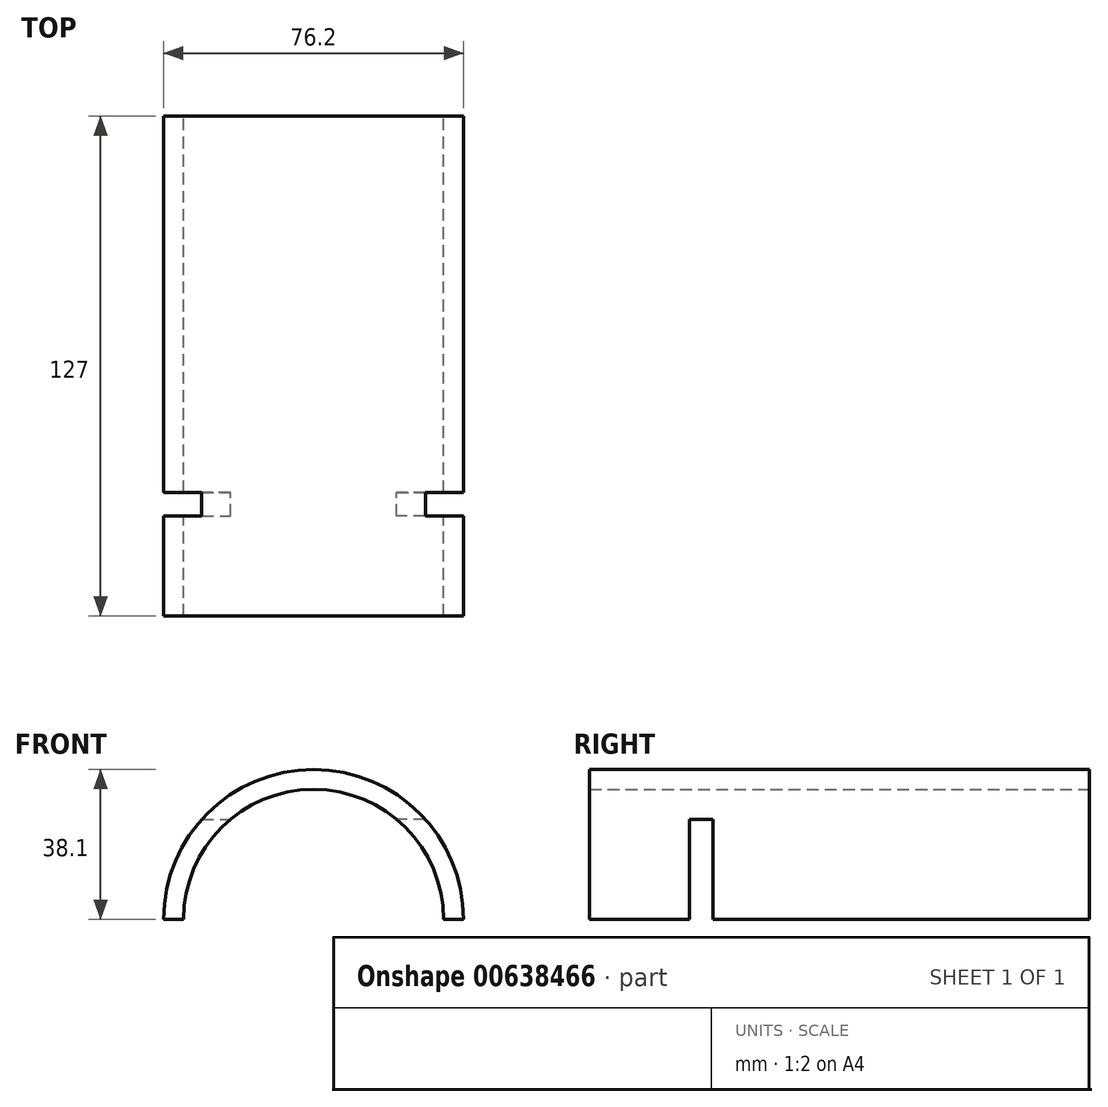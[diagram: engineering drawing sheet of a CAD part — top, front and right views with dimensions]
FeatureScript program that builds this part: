
annotation { "Feature Type Name" : "Feature", "Feature Type Description" : "" }
export const myFeature = defineFeature(function(context is Context, id is Id, definition is map)
    precondition{}
    {
        {
            var Q0;
            Q0=qCreatedBy(makeId("Front.planeOp"),FACE);
            var sketch = newSketch(context, id + "F0", { "sketchPlane" : qUnion([Q0])});
            skArc(sketch, "E0", {"start": v(38.1, 0) * mm, "mid": v(0, 38.1) * mm, "end": v(-38.1, 0) * mm});
            skArc(sketch, "E1", {"start": v(33.02, 0) * mm, "mid": v(0, 33.02) * mm, "end": v(-33.02, 0) * mm});
            skLineSegment(sketch, "E2", {"start": v(-38.1, 0) * mm, "end": v(-33.02, 0) * mm});
            skLineSegment(sketch, "E3", {"start": v(33.02, 0) * mm, "end": v(38.1, 0) * mm});
            skSolve(sketch);
        }
        {
            var Q0;
            Q0 = qSketchRegion(id + "F0", true);
            extrude(context, id + "F1", {"entities" : qUnion([Q0]), "depth" : 127 * mm, "offsetDistance" : 25.4 * mm});
        }
        {
            var Q0;
            Q0=qCreatedBy(makeId("Right.planeOp"),FACE);
            var sketch = newSketch(context, id + "F2", { "sketchPlane" : qUnion([Q0])});
            skLineSegment(sketch, "E4", {"start": v(-101.6, 0) * mm, "end": v(-101.6, 25.4) * mm});
            skLineSegment(sketch, "E5", {"start": v(-101.6, 25.4) * mm, "end": v(-95.6, 25.4) * mm});
            skLineSegment(sketch, "E6", {"start": v(-95.6, 25.4) * mm, "end": v(-95.6, 0) * mm});
            skLineSegment(sketch, "E7", {"start": v(-95.6, 0) * mm, "end": v(-101.6, 0) * mm});
            skSolve(sketch);
        }
        {
            var Q0;
            Q0 = qSketchRegion(id + "F2", true);
            extrude(context, id + "F3", {"entities" : qUnion([Q0]), "operationType" : NewBodyOperationType.REMOVE, "oppositeDirection" : true, "depth" : 101.6 * mm, "offsetDistance" : 25.4 * mm});
        }
        {
            var Q0;
            Q0 = qSketchRegion(id + "F2", true);
            extrude(context, id + "F4", {"entities" : qUnion([Q0]), "operationType" : NewBodyOperationType.REMOVE, "depth" : 101.6 * mm, "offsetDistance" : 25.4 * mm});
        }
    });
